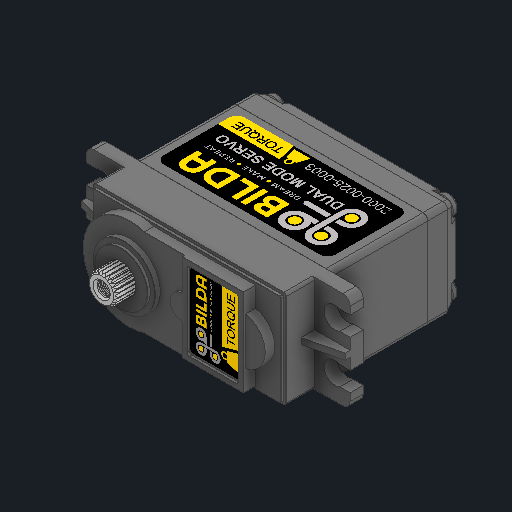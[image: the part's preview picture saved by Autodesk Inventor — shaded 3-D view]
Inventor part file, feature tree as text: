
AUTODESK INVENTOR PART (.ipt)
format: ipt  version: 2023 (Build 270158000, 158)  size: 1,927,680 bytes
history: native  units: in
note: dims shown in document units (in); Inventor stores cm internally (conversion verified against a paired STEP export)
features: other x6, sketch x2
ambient origin geometry x8: Origin, YZ Plane, XZ Plane, XY Plane, X Axis, Y Axis, Z Axis, Center Point
bodies: Solid1 (feature_tree), Solid2 (feature_tree)
feature tree (8):
  parser-record x1  (decoder bookkeeping rows leaked as tree rows — omitted from the tree; the rows remain in map.json)
  sketch  "Sketch1"
  sketch  "Sketch2"
  other  "Decal1"
  other  "Decal2"
  other  "Image3"
  other  "Image4"
  other  "Join1[1]"
